# Revit family: QF_ELECTROLUXPROFESSIONAL_1LSNTJ_WN6-8_E
name_source: partatom
category: Attrezzature speciali
units: mm (PartAtom-declared; Revit-internal decimal feet)

## family parameters
Basato su piano di lavoro = No
Condiviso = No
Punto di calcolo locali = No
Quota connettore circolare = Usa diametro
Sempre verticale = Sì
Taglio con vuoti quando caricato = No
Tipo di parte = Normale

## types (24) — shared parameters
Depth = 682.4 mm  [stored 2.23885 ft]
Depth Actual = 680 mm  [stored 2.23097 ft]
Height = 1134.3 mm  [stored 3.72146 ft]
Height Actual = 1135 mm  [stored 3.72375 ft]
Latent Heat Output = 0.0
Length Actual = 660 mm  [stored 2.16535 ft]
Modello = WN6-8
Produttore = Electrolux Professional
Sensible Heat Output = 0.0
URL = www.electroluxprofessional.com
Weight = 116
Width = 660 mm  [stored 2.16535 ft]
zero-valued in all types: Gas KW, Prospetto di default, Steam Pounds per Hour

## per-type parameters (varying)
| type | Cycle | Descrizione | Item Number | Phase | Volts | Watts |
| 9867630198 | 50 Hz | WASHER WN6-8 8KG EL 7,5KW 380-415/50/3 COMPASS PRO 6G07 ML 2xWATER POWDER+5xLIQ. VALV.OPEN SILVER 2.I/O TRAFO DISCON. ST | 1L0GET | 3 | 415 V | 7800 W |
| 9867630130 | 60 Hz | WASHER WN6-8 8KG EL 7,5KW 440/60/3 COMPASS PRO 6G01 ML 2xWATER POWDER VALV.OPEN SST/SILVER TRAFO DISCON. STOP | 1L823J | 3 | 440 V | 7900 W |
| 9867630323 | 60 Hz | WASHER WN6-8 8KG EL 5,4KW 220-240/60/1 COMPASS PRO 6G07 ML 2xWATER POWDER+5xLIQ. VALV.OPEN SILVER 2.I/O DISCON. STOP | 1LT6DF | 1 | 240 V | 5700 W |
| 9867630252 | 50 Hz | WASHER WN6-8 8KG EL 7,5KW 380-415/50/3N COMPASS PRO 6L01 ML 2xWATER POWDER VALV.OPEN SILVER DISCON. | 1L0GUP | 3 | 415 V | 7800 W |
| 9867630135 | 50 Hz | WASHER WN6-8 8KG EL 7,5KW 380-415/50/3N COMPASS PRO 6A01 ML 2xWATER POWDER+5xLIQ. EL.VALV.OPEN SILVER 2.I/O DISCON. | 1LA1AU | 3 | 415 V | 7800 W |
| 9867630069 | 50 Hz | WASHER WN6-8 8KG NO HEAT 200/50/60/3 COMPASS PRO 6G41 JP,EN 2xWATER POWDER+5xLIQ. VALV.OPEN SST/SILVER SL.DRUM 2.I/O DIS | 1L0G8G | 3 | 200 V | 500 W |
| 9867630235 | 60 Hz | WASHER WN6-8 8KG EL 7,5KW 220-240/60/3 COMPASS PRO 6G01 ML 2xWATER POWDER+5xLIQ. VALV.OPEN SILVER 2.I/O QC DISCON. STOP | 1L0GLH | 3 | 240 V | 7800 W |
| 9867630132 | 60 Hz | WASHER WN6-8 8KG EL 7,5KW 440/60/3 COMPASS PRO 6G01 ML 2xWATER POWDER VALV.OPEN SILVER TRAFO DISCON. STOP | 1L823L | 3 | 440 V | 7900 W |
| 9867630177 | 50 Hz | WASHER WN6-8 8KG EL 4,1KW 200/50/60/3 COMPASS PRO 6G41 JP,EN 2xWATER POWDER+5xLIQ. VALV.OPEN SST/SILVER SL.DRUM 2.I/O DI | 1LA1AV | 3 | 200 V | 4400 W |
| 9867630258 | 50 Hz | WASHER WN6-8 8KG EL 7,5KW 380-415/50/3N COMPASS PRO 6H12 ML 2xWATER POWDER+5xLIQ. VALV.OPEN SILVER SL.DRUM 2.I/O DISCON. | 1L0GV9 | 3 | 415 V | 7800 W |
| 9867630278 | 60 Hz | WASHER WN6-8 8KG EL 7,5KW 220-240/60/1N COMPASS PRO 6G07 ML 2xWATER POWDER+5xLIQ. VALV.OPEN SILVER 2.I/O DISCON. STOP | 1LSPP1 | 1 | 240 V | 7800 W |
| 9867630263 | 50 Hz | WASHER WN6-8 8KG EL 7,5KW 220-240/50/3 COMPASS PRO 6G01 ML 2xWATER POWDER+5xLIQ. VALV.OPEN SILVER 2.I/O QC DISCON. STOP | 1LSPHH | 3 | 240 V | 7800 W |
| 9867630134 | 50 Hz | WASHER WN6-8 8KG EL 7,5KW 380-415/220-240/50/3N/3 COMPASS PRO 6G01 ML 2xWATER POWDER+5xLIQ. VALV.OPEN SILVER 2.I/O DISCO | 1LSP3D | 3 | 415 V | 7800 W |
| 9867630286 | 60 Hz | WASHER WN6-8 8KG EL 7,5KW 220-240/60/3 COMPASS PRO 6G07 SE 2xWATER POWDER+5xLIQ. VALV.OPEN SST 2.I/O DISCON. STOP | 1LSPSA | 3 | 240 V | 7800 W |
| 9867630256 | 50 Hz | WASHER WN6-8 8KG EL 7,5KW 380-415/50/3N COMPASS PRO 6G01 ML 2xWATER POWDER+5xLIQ. VALV.OPEN SST/SILVER 2.I/O DISCON. STO | 1LA24G | 3 | 415 V | 7800 W |
| 9867630199 | 60 Hz | WASHER WN6-8 8KG LE 3KW 220-240/60/1N COMPASS PRO 6G07 ML 2xWATER POWDER VALV.OPEN SST/SILVER DISCON. STOP | 1L0GEU | 1 | 240 V | 3300 W |
| 9867630131 | 50 Hz | WASHER WN6-8 8KG NO HEAT 220-240/50/1N COMPASS PRO 6L01 ML 2xWATER POWDER+5xLIQ. VALV.OPEN SILVER EXT.PM. 2.I/O DISCON. | 1L823K | 1 | 240 V | 400 W |
| 9867630136 | 50 Hz | WASHER WN6-8 8KG NO HEAT 220-240/50/1N COMPASS PRO 6G05 ML 2xWATER POWDER+5xLIQ. VALV.OPEN SST/SILVER 2.I/O DISCON. STOP | 1L823M | 1 | 240 V | 400 W |
| 9867630254 | 50 Hz | WASHER WN6-8 8KG EL 7,5KW 380-415/50/3 COMPASS PRO 6G07 ML 2xWATER POWDER VALV.OPEN SST/SILVER TRAFO DISCON. STOP | 1LA23T | 3 | 415 V | 7800 W |
| 9867630183 | 50 Hz | WASHER WN6-8 8KG EL 7,5KW 380-415/50/3N COMPASS PRO 6H01 ML 2xWATER POWDER+5xLIQ. VALV.OPEN SST/SILVER 2.I/O DISCON. STO | 1LSP9J | 3 | 415 V | 7800 W |
| 9867630193 | 50 Hz | WASHER WN6-8 8KG EL 7,5KW 380-415/50/3N COMPASS PRO 6G01 ML 2xWATER POWDER VALV.OPEN SILVER DISCON. STOP | 1L0GEM | 3 | 415 V | 7800 W |
| 9867630287 | 60 Hz | WASHER WN6-8 8KG EL 7,5KW 208-240/60/3 COMPASS PRO 6G07 ML 2xWATER POWDER+5xLIQ. VALV.OPEN SST 2.I/O DISCON. STOP | 1L82AZ | 3 | 240 V | 7800 W |
| 9867630133 | 60 Hz | WASHER WN6-8 8KG EL 7,5KW 440/60/3 COMPASS PRO 6G07 ML 2xWATER POWDER+5xLIQ. VALV.OPEN SILVER 2.I/O TRAFO DISCON. STOP | 1LSP5A | 3 | 440 V | 7900 W |
| 9867630180 | 60 Hz | WASHER WN6-8 8KG EL 7KW 115/60/3 COMPASS PRO 6G07 ML 2xWATER POWDER+5xLIQ. VALV.OPEN SILVER 2.I/O TRAFO DISCON. STOP | 1LA1BK | 3 | 115 V | 7200 W |

note: [stored X ft] marks values corroborated as IEEE doubles in the binary element streams (Revit-internal decimal feet)

## geometry (parser evidence)
native form markers: Sweep x4
no freeform markers — native parametric forms only
